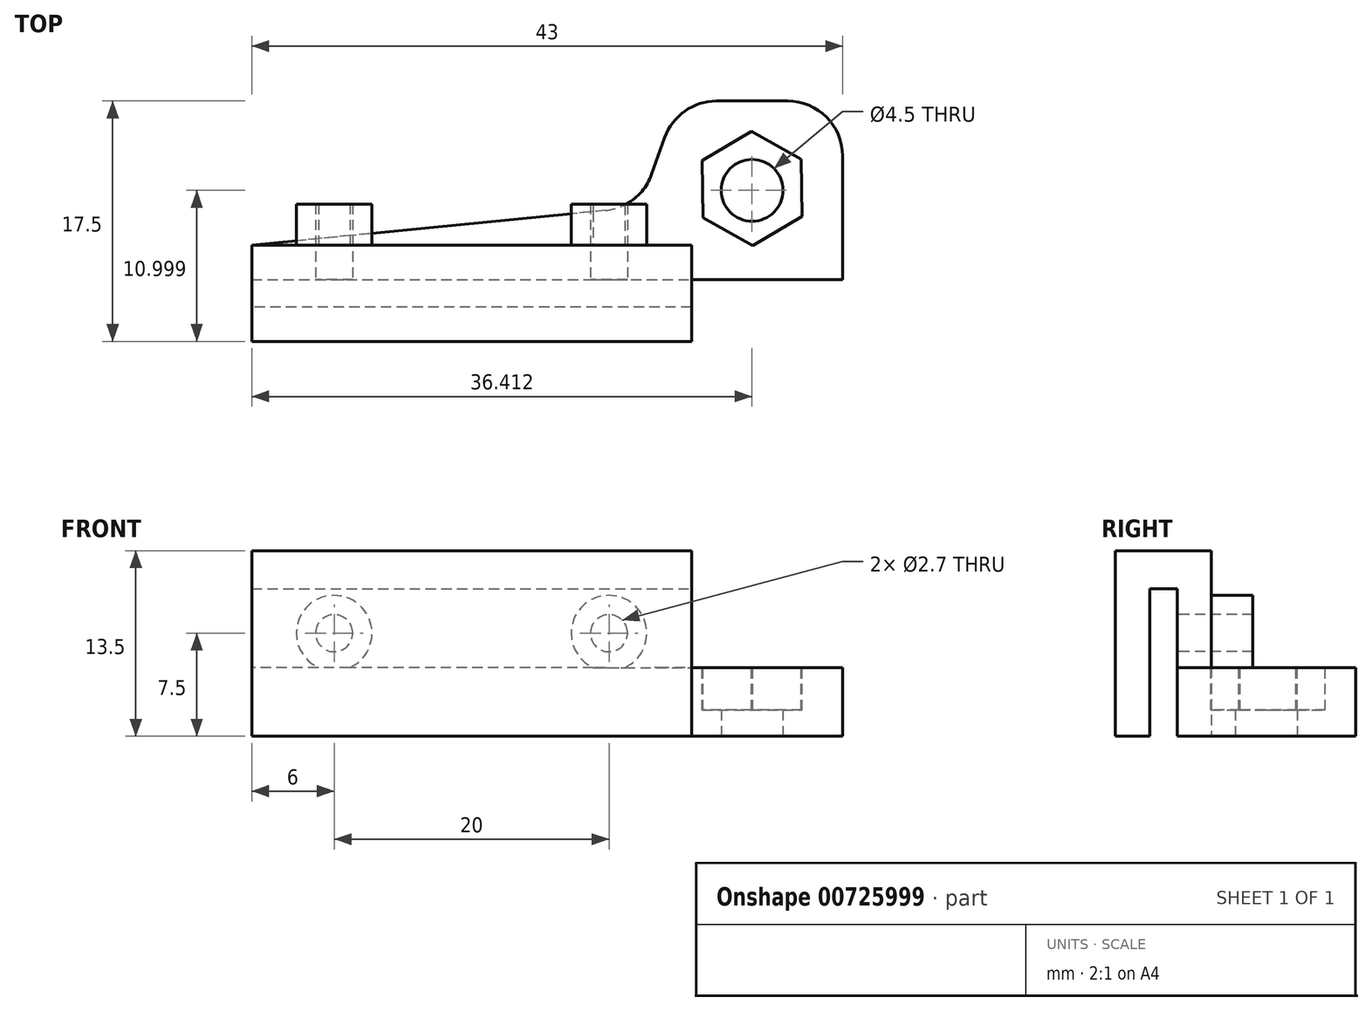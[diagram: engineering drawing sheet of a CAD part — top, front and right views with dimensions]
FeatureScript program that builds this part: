
annotation { "Feature Type Name" : "Feature", "Feature Type Description" : "" }
export const myFeature = defineFeature(function(context is Context, id is Id, definition is map)
    precondition{}
    {
        {
            var Q0;
            Q0=qCreatedBy(makeId("Top.planeOp"),FACE);
            var sketch = newSketch(context, id + "F0", { "sketchPlane" : qUnion([Q0])});
            skLineSegment(sketch, "E0", {"start": v(0, 0) * mm, "end": v(43, 0) * mm});
            skLineSegment(sketch, "E1", {"start": v(43, 0) * mm, "end": v(43, 9) * mm});
            skLineSegment(sketch, "E2", {"start": v(39, 13) * mm, "end": v(33.82, 13) * mm});
            skLineSegment(sketch, "E3", {"start": v(30.05, 10.34) * mm, "end": v(29.1, 7.67) * mm});
            skLineSegment(sketch, "E4", {"start": v(25.73, 5.03) * mm, "end": v(0, 2.5) * mm});
            skLineSegment(sketch, "E5", {"start": v(0, 2.5) * mm, "end": v(0, 0) * mm});
            skPoint(sketch, "E6.cCircle.centerSnap0", {"position": v(37, 13) * mm});
            skPoint(sketch, "E6.cCircle.centerSnap1", {"position": v(43, 6.5) * mm});
            skPoint(sketch, "E7.visualSharp", {"position": v(31, 13) * mm});
            skArc(sketch, "E7.filletArc", {"start": v(33.82, 13) * mm, "mid": v(31.52, 12.27) * mm, "end": v(30.05, 10.34) * mm});
            skPoint(sketch, "E8.visualSharp", {"position": v(43, 13) * mm});
            skArc(sketch, "E8.filletArc", {"start": v(43, 9) * mm, "mid": v(41.83, 11.83) * mm, "end": v(39, 13) * mm});
            skLineSegment(sketch, "E9", {"start": v(0, -4.08) * mm, "end": v(23.91, -4.08) * mm, "construction": true});
            skPoint(sketch, "E10.visualSharp", {"position": v(28.26, 5.28) * mm});
            skArc(sketch, "E10.filletArc", {"start": v(25.73, 5.03) * mm, "mid": v(27.8, 5.86) * mm, "end": v(29.1, 7.67) * mm});
            skSolve(sketch);
        }
        {
            var Q0;
            Q0=makeQuery(id+"F0.imprint","IMPRINT",FACE,{"disambiguationData":[TD([[makeQuery(id+"F0.imprint","IMPRINT",EDGE,{"derivedFrom":sQuery(id+"F0.wireOp",EDGE,"E0")}),1.0]])]});
            var Q1;
            Q1=makeQuery(id+"F0.imprint","IMPRINT",FACE,{"disambiguationData":[TD([[makeQuery(id+"F0.imprint","IMPRINT",EDGE,{"derivedFrom":sQuery(id+"F0.wireOp",EDGE,"9723bb3a-2dcc-4b88-a40a-11d1b5373118.0")}),-1.0]])]});
            extrude(context, id + "F1", {"entities" : qUnion([Q0, Q1]), "depth" : 5 * mm, "offsetDistance" : 25 * mm});
        }
        {
            var Q0;
            Q0=makeQuery(id+"F1.opExtrude","CAP_FACE",FACE,{"disambiguationData":[OSD([sQuery(id+"F0.wireOp",EDGE,"E0"),sQuery(id+"F0.wireOp",EDGE,"E1"),sQuery(id+"F0.wireOp",EDGE,"E2"),sQuery(id+"F0.wireOp",EDGE,"E3"),sQuery(id+"F0.wireOp",EDGE,"E4"),sQuery(id+"F0.wireOp",EDGE,"E5"),sQuery(id+"F0.wireOp",EDGE,"E7.filletArc"),sQuery(id+"F0.wireOp",EDGE,"E8.filletArc"),sQuery(id+"F0.wireOp",EDGE,"E10.filletArc")])],"isStart":false});
            var sketch = newSketch(context, id + "F2", { "sketchPlane" : qUnion([Q0])});
            skCircle(sketch, "E11.cCircle", {"center": v(36.41, 6.63) * mm, "radius": 3.6 * mm, "construction": true});
            skPoint(sketch, "E11.cCircle.centerSnap0", {"position": v(43, 4.5) * mm});
            skPoint(sketch, "E11.cCircle.centerSnap1", {"position": v(36.41, 13) * mm});
            skLineSegment(sketch, "E11.0", {"start": v(36.36, 10.78) * mm, "end": v(39.98, 8.75) * mm});
            skLineSegment(sketch, "E11.1", {"start": v(39.98, 8.75) * mm, "end": v(40.04, 4.6) * mm});
            skLineSegment(sketch, "E11.2", {"start": v(40.04, 4.6) * mm, "end": v(36.47, 2.47) * mm});
            skLineSegment(sketch, "E11.3", {"start": v(36.47, 2.47) * mm, "end": v(32.84, 4.5) * mm});
            skLineSegment(sketch, "E11.4", {"start": v(32.84, 4.5) * mm, "end": v(32.79, 8.66) * mm});
            skLineSegment(sketch, "E11.5", {"start": v(32.79, 8.66) * mm, "end": v(36.36, 10.78) * mm});
            skPoint(sketch, "E11.0.midPoint", {"position": v(38.17, 9.77) * mm});
            skSolve(sketch);
        }
        {
            var Q0;
            Q0=makeQuery(id+"F2.imprint","IMPRINT",FACE,{"disambiguationData":[TD([[makeQuery(id+"F2.imprint","IMPRINT",EDGE,{"derivedFrom":sQuery(id+"F2.wireOp",EDGE,"E11.0")}),-1.0]])]});
            extrude(context, id + "F3", {"entities" : qUnion([Q0]), "operationType" : NewBodyOperationType.REMOVE, "oppositeDirection" : true, "depth" : 3.1 * mm, "offsetDistance" : 25 * mm});
        }
        {
            var Q0;
            Q0=makeQuery(id+"F1.opExtrude","CAP_FACE",FACE,{"disambiguationData":[OSD([sQuery(id+"F0.wireOp",EDGE,"E0"),sQuery(id+"F0.wireOp",EDGE,"E1"),sQuery(id+"F0.wireOp",EDGE,"E2"),sQuery(id+"F0.wireOp",EDGE,"E3"),sQuery(id+"F0.wireOp",EDGE,"E4"),sQuery(id+"F0.wireOp",EDGE,"E5"),sQuery(id+"F0.wireOp",EDGE,"E7.filletArc"),sQuery(id+"F0.wireOp",EDGE,"E8.filletArc"),sQuery(id+"F0.wireOp",EDGE,"E10.filletArc")])],"isStart":true});
            var sketch = newSketch(context, id + "F4", { "sketchPlane" : qUnion([Q0])});
            skCircle(sketch, "E12", {"center": v(36.41, -6.5) * mm, "radius": 2.25 * mm});
            skPoint(sketch, "E12.centerSnap0", {"position": v(43, -4.5) * mm});
            skPoint(sketch, "E12.centerSnap1", {"position": v(36.41, -13) * mm});
            skLineSegment(sketch, "E13", {"start": v(36.41, -13) * mm, "end": v(36.41, 1.7) * mm, "construction": true});
            skLineSegment(sketch, "E14", {"start": v(36.41, -6.5) * mm, "end": v(42.46, -6.5) * mm, "construction": true});
            skLineSegment(sketch, "E15", {"start": v(42.58, 0) * mm, "end": v(43, 0) * mm, "construction": true});
            skLineSegment(sketch, "E16", {"start": v(42.58, 0) * mm, "end": v(42.46, -6.5) * mm, "construction": true});
            skSolve(sketch);
        }
        {
            var Q0;
            Q0=makeQuery(id+"F4.imprint","IMPRINT",FACE,{"disambiguationData":[TD([[makeQuery(id+"F4.imprint","IMPRINT",EDGE,{"derivedFrom":sQuery(id+"F4.wireOp",EDGE,"E12")}),1.0]])]});
            extrude(context, id + "F5", {"entities" : qUnion([Q0]), "operationType" : NewBodyOperationType.REMOVE, "endBound" : BoundingType.THROUGH_ALL, "oppositeDirection" : true, "depth" : 25 * mm, "offsetDistance" : 25 * mm});
        }
        {
            var Q0;
            Q0=makeQuery(id+"F1.opExtrude","CAP_FACE",FACE,{"disambiguationData":[OSD([sQuery(id+"F0.wireOp",EDGE,"E0"),sQuery(id+"F0.wireOp",EDGE,"E1"),sQuery(id+"F0.wireOp",EDGE,"E2"),sQuery(id+"F0.wireOp",EDGE,"E3"),sQuery(id+"F0.wireOp",EDGE,"E4"),sQuery(id+"F0.wireOp",EDGE,"E5"),sQuery(id+"F0.wireOp",EDGE,"E7.filletArc"),sQuery(id+"F0.wireOp",EDGE,"E8.filletArc"),sQuery(id+"F0.wireOp",EDGE,"E10.filletArc")])],"isStart":false});
            var sketch = newSketch(context, id + "F6", { "sketchPlane" : qUnion([Q0])});
            skLineSegment(sketch, "E17", {"start": v(0, 2.5) * mm, "end": v(32, 2.5) * mm});
            skLineSegment(sketch, "E18", {"start": v(32, 2.5) * mm, "end": v(32, 0) * mm});
            skSolve(sketch);
        }
        {
            var Q0;
            Q0=makeQuery(id+"F6.imprint","IMPRINT",FACE,{"disambiguationData":[TD([[makeQuery(id+"F6.imprint","IMPRINT",EDGE,{"derivedFrom":sQuery(id+"F6.wireOp",EDGE,"E17")}),-1.0]])]});
            extrude(context, id + "F7", {"entities" : qUnion([Q0]), "operationType" : NewBodyOperationType.ADD, "depth" : 8.5 * mm, "offsetDistance" : 25 * mm});
        }
        {
            var Q0;
            {var subQ0=sQuery(id+"F0.wireOp",EDGE,"E0");Q0=makeQuery(id+"F7.boolean.opBoolean","MERGE",FACE,{"derivedFrom":[makeQuery(id+"F1.opExtrude","SWEPT_FACE",FACE,{"disambiguationData":[OSD([subQ0])]}),makeQuery(id+"F7.opExtrude","SWEPT_FACE",FACE,{"disambiguationData":[OSD([subQ0])]})]});}
            var sketch = newSketch(context, id + "F8", { "sketchPlane" : qUnion([Q0])});
            skLineSegment(sketch, "E19.bottom", {"start": v(0, 13.5) * mm, "end": v(32, 13.5) * mm});
            skLineSegment(sketch, "E19.top", {"start": v(0, 10.75) * mm, "end": v(32, 10.75) * mm});
            skLineSegment(sketch, "E19.left", {"start": v(0, 13.5) * mm, "end": v(0, 10.75) * mm});
            skLineSegment(sketch, "E19.right", {"start": v(32, 13.5) * mm, "end": v(32, 10.75) * mm});
            skSolve(sketch);
        }
        {
            var Q0;
            Q0=makeQuery(id+"F8.imprint","IMPRINT",FACE,{"disambiguationData":[TD([[makeQuery(id+"F8.imprint","IMPRINT",EDGE,{"derivedFrom":sQuery(id+"F8.wireOp",EDGE,"E19.bottom")}),-1.0]])]});
            extrude(context, id + "F9", {"entities" : qUnion([Q0]), "operationType" : NewBodyOperationType.ADD, "depth" : 4.5 * mm, "offsetDistance" : 25 * mm});
        }
        {
            var Q0;
            Q0=makeQuery(id+"F9.opExtrude","SWEPT_FACE",FACE,{"disambiguationData":[OSD([sQuery(id+"F8.wireOp",EDGE,"E19.top")])]});
            var sketch = newSketch(context, id + "F10", { "sketchPlane" : qUnion([Q0])});
            skLineSegment(sketch, "E20.bottom", {"start": v(32, 4.5) * mm, "end": v(0, 4.5) * mm});
            skLineSegment(sketch, "E20.top", {"start": v(32, 2) * mm, "end": v(0, 2) * mm});
            skLineSegment(sketch, "E20.left", {"start": v(32, 4.5) * mm, "end": v(32, 2) * mm});
            skLineSegment(sketch, "E20.right", {"start": v(0, 4.5) * mm, "end": v(0, 2) * mm});
            skSolve(sketch);
        }
        {
            var Q0;
            Q0=makeQuery(id+"F10.imprint","IMPRINT",FACE,{"disambiguationData":[TD([[makeQuery(id+"F10.imprint","IMPRINT",EDGE,{"derivedFrom":sQuery(id+"F10.wireOp",EDGE,"E20.bottom")}),-1.0]])]});
            extrude(context, id + "F11", {"entities" : qUnion([Q0]), "operationType" : NewBodyOperationType.ADD, "depth" : (13.5 - 2.75) * mm, "offsetDistance" : 25 * mm});
        }
        {
            var Q0;
            Q0=makeQuery(id+"F7.opExtrude","SWEPT_FACE",FACE,{"disambiguationData":[OSD([sQuery(id+"F6.wireOp",EDGE,"E17")])]});
            var sketch = newSketch(context, id + "F12", { "sketchPlane" : qUnion([Q0])});
            skArc(sketch, "E21", {"start": v(-4.85, 5) * mm, "mid": v(-6, 10.25) * mm, "end": v(-7.15, 5) * mm});
            skArc(sketch, "E22", {"start": v(-24.85, 5) * mm, "mid": v(-26, 10.25) * mm, "end": v(-27.15, 5) * mm});
            skCircle(sketch, "E23", {"center": v(-6, 7.5) * mm, "radius": 1.35 * mm});
            skCircle(sketch, "E24", {"center": v(-26, 7.5) * mm, "radius": 1.35 * mm});
            skLineSegment(sketch, "E25", {"start": v(-32, 5) * mm, "end": v(0, 5) * mm, "construction": true});
            skSolve(sketch);
        }
        {
            var Q0;
            Q0=makeQuery(id+"F12.imprint","IMPRINT",FACE,{"disambiguationData":[TD([[makeQuery(id+"F12.imprint","IMPRINT",EDGE,{"derivedFrom":sQuery(id+"F12.wireOp",EDGE,"E22")}),1.0]])]});
            var Q1;
            Q1=makeQuery(id+"F12.imprint","IMPRINT",FACE,{"disambiguationData":[TD([[makeQuery(id+"F12.imprint","IMPRINT",EDGE,{"derivedFrom":sQuery(id+"F12.wireOp",EDGE,"E21")}),1.0]])]});
            extrude(context, id + "F13", {"entities" : qUnion([Q0, Q1]), "operationType" : NewBodyOperationType.ADD, "depth" : 3 * mm, "offsetDistance" : 25 * mm});
        }
        {
            var Q0;
            Q0=makeQuery(id+"F13.boolean.opBoolean","SPLIT",FACE,{"disambiguationData":[TD([makeQuery(id+"F13.opExtrude","SWEPT_FACE",FACE,{"disambiguationData":[OSD([sQuery(id+"F12.wireOp",EDGE,"E23")])]})])],"derivedFrom":makeQuery(id+"F7.opExtrude","SWEPT_FACE",FACE,{"disambiguationData":[OSD([sQuery(id+"F6.wireOp",EDGE,"E17")])]})});
            var Q1;
            Q1=makeQuery(id+"F13.boolean.opBoolean","SPLIT",FACE,{"disambiguationData":[TD([makeQuery(id+"F13.opExtrude","SWEPT_FACE",FACE,{"disambiguationData":[OSD([sQuery(id+"F12.wireOp",EDGE,"E24")])]})])],"derivedFrom":makeQuery(id+"F7.opExtrude","SWEPT_FACE",FACE,{"disambiguationData":[OSD([sQuery(id+"F6.wireOp",EDGE,"E17")])]})});
            extrude(context, id + "F14", {"entities" : qUnion([Q0, Q1]), "operationType" : NewBodyOperationType.REMOVE, "endBound" : BoundingType.UP_TO_NEXT, "oppositeDirection" : true, "depth" : 25 * mm, "offsetDistance" : 25 * mm});
        }
    });
